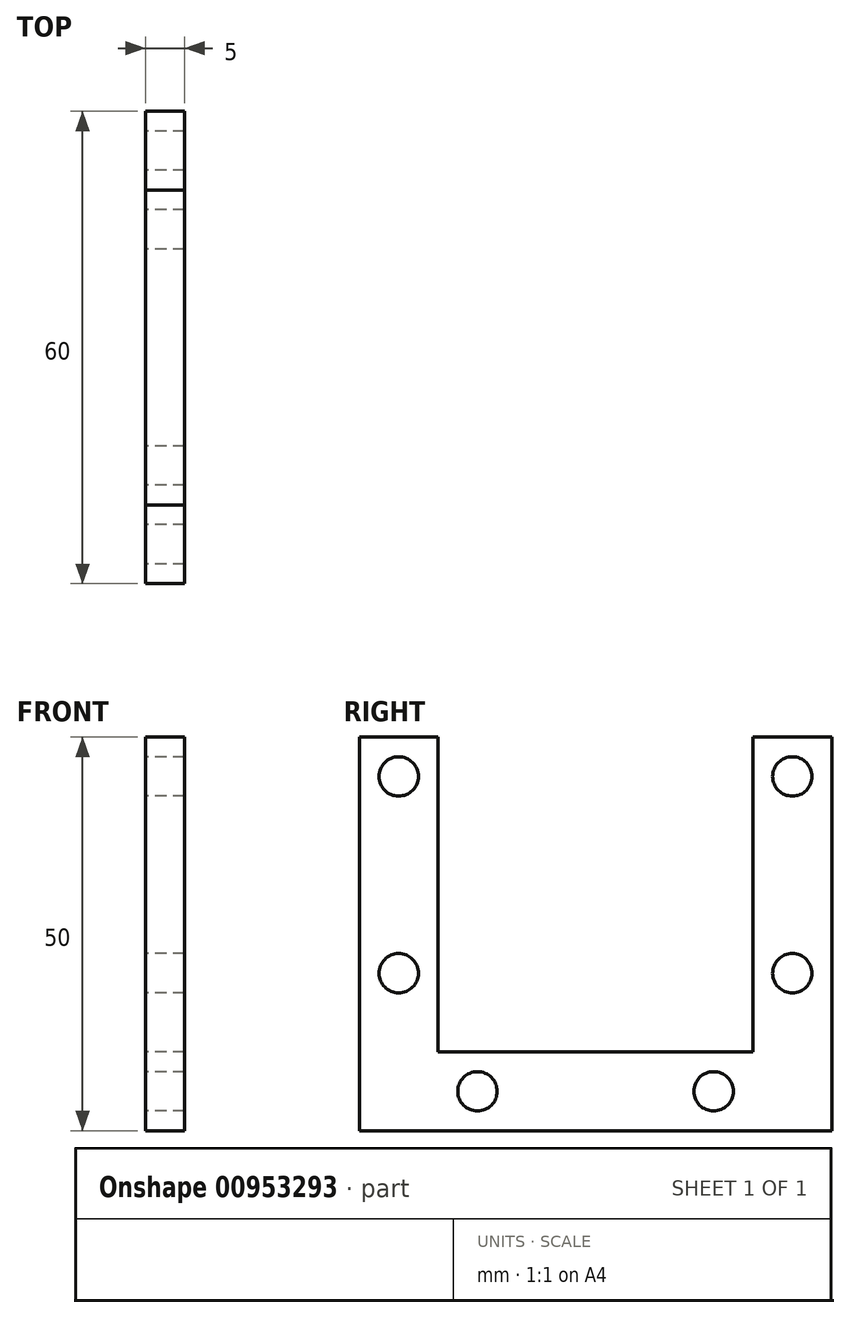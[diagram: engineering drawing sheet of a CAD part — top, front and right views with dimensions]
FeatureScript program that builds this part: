
annotation { "Feature Type Name" : "Feature", "Feature Type Description" : "" }
export const myFeature = defineFeature(function(context is Context, id is Id, definition is map)
    precondition{}
    {
        {
            var Q0;
            Q0=qCreatedBy(makeId("Right.planeOp"),FACE);
            var sketch = newSketch(context, id + "F0", { "sketchPlane" : qUnion([Q0])});
            skLineSegment(sketch, "E0", {"start": v(-26.24, 50) * mm, "end": v(-26.24, 0) * mm});
            skLineSegment(sketch, "E1", {"start": v(-26.24, 0) * mm, "end": v(33.76, 0) * mm});
            skLineSegment(sketch, "E2", {"start": v(33.76, 0) * mm, "end": v(33.76, 50) * mm});
            skLineSegment(sketch, "E3", {"start": v(33.76, 50) * mm, "end": v(23.76, 50) * mm});
            skLineSegment(sketch, "E4", {"start": v(23.76, 50) * mm, "end": v(23.76, 10) * mm});
            skLineSegment(sketch, "E5", {"start": v(23.76, 10) * mm, "end": v(-16.24, 10) * mm});
            skLineSegment(sketch, "E6", {"start": v(-16.24, 10) * mm, "end": v(-16.24, 50) * mm});
            skLineSegment(sketch, "E7", {"start": v(-26.24, 50) * mm, "end": v(-16.24, 50) * mm});
            skCircle(sketch, "E8", {"center": v(-11.24, 5) * mm, "radius": 2.5 * mm});
            skCircle(sketch, "E9", {"center": v(18.76, 5) * mm, "radius": 2.5 * mm});
            skCircle(sketch, "E10", {"center": v(-21.24, 45) * mm, "radius": 2.5 * mm});
            skCircle(sketch, "E11", {"center": v(-21.24, 20) * mm, "radius": 2.5 * mm});
            skCircle(sketch, "E12", {"center": v(28.76, 45) * mm, "radius": 2.5 * mm});
            skCircle(sketch, "E13", {"center": v(28.76, 20) * mm, "radius": 2.5 * mm});
            skSolve(sketch);
        }
        {
            var Q0;
            Q0 = qSketchRegion(id + "F0", true);
            extrude(context, id + "F1", {"entities" : qUnion([Q0]), "depth" : 5 * mm, "offsetDistance" : 25 * mm});
        }
    });
